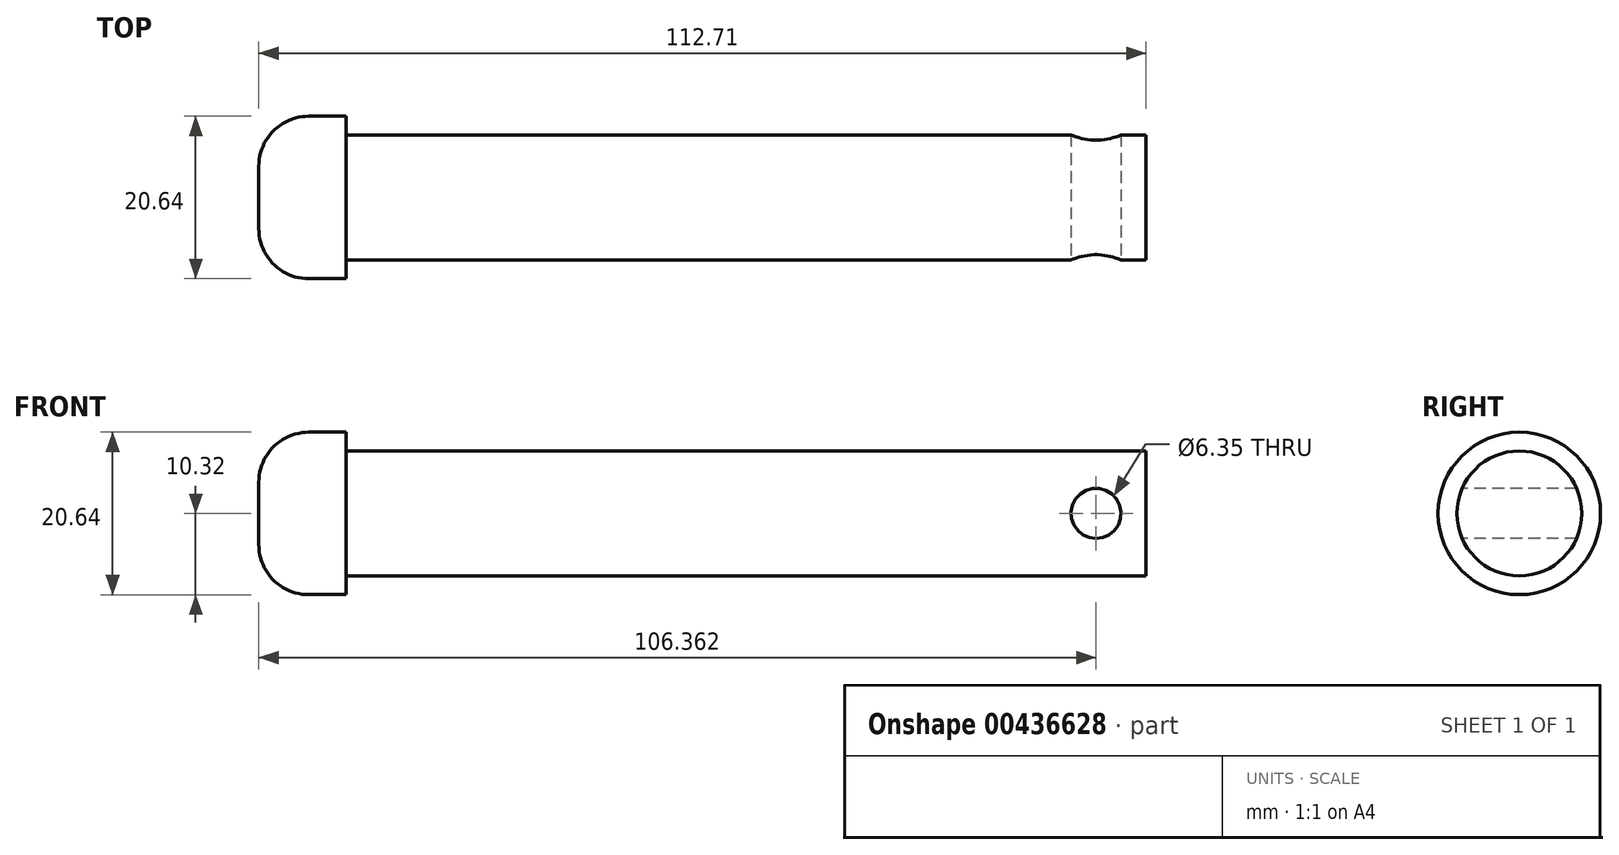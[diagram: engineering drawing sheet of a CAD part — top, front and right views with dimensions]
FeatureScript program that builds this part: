
annotation { "Feature Type Name" : "Feature", "Feature Type Description" : "" }
export const myFeature = defineFeature(function(context is Context, id is Id, definition is map)
    precondition{}
    {
        {
            var Q0;
            Q0=qCreatedBy(makeId("Front.planeOp"),FACE);
            var sketch = newSketch(context, id + "F0", { "sketchPlane" : qUnion([Q0])});
            skLineSegment(sketch, "E0", {"start": v(0, 3.97) * mm, "end": v(0, 0) * mm});
            skLineSegment(sketch, "E1", {"start": v(6.35, 10.32) * mm, "end": v(11.11, 10.32) * mm});
            skLineSegment(sketch, "E2", {"start": v(11.11, 10.32) * mm, "end": v(11.11, 7.94) * mm});
            skLineSegment(sketch, "E3", {"start": v(11.11, 7.94) * mm, "end": v(112.71, 7.94) * mm});
            skLineSegment(sketch, "E4", {"start": v(112.71, 7.94) * mm, "end": v(112.71, 0) * mm});
            skLineSegment(sketch, "E5", {"start": v(-31.62, 0) * mm, "end": v(102.7, 0) * mm, "construction": true});
            skPoint(sketch, "E6.visualSharp", {"position": v(0, 10.32) * mm});
            skArc(sketch, "E6.filletArc", {"start": v(6.35, 10.32) * mm, "mid": v(1.86, 8.46) * mm, "end": v(0, 3.97) * mm});
            skLineSegment(sketch, "E7", {"start": v(0, 0) * mm, "end": v(112.71, 0) * mm});
            skSolve(sketch);
        }
        {
            var Q0;
            Q0=makeQuery(id+"F0.imprint","IMPRINT",FACE,{"disambiguationData":[TD([[makeQuery(id+"F0.imprint","IMPRINT",EDGE,{"derivedFrom":sQuery(id+"F0.wireOp",EDGE,"E0")}),1.0]])]});
            var Q1;
            Q1=sQuery(id+"F0.wireOp",EDGE,"E5");
            revolve(context, id + "F1", {"surfaceOperationType" : NewSurfaceOperationType.NEW, "entities" : qUnion([Q0]), "axis" : qUnion([Q1]), "revolveType" : RevolveType.FULL});
        }
        {
            var Q0;
            Q0=qCreatedBy(makeId("Front.planeOp"),FACE);
            var sketch = newSketch(context, id + "F2", { "sketchPlane" : qUnion([Q0])});
            skCircle(sketch, "E8", {"center": v(106.36, 0) * mm, "radius": 3.17 * mm});
            skSolve(sketch);
        }
        {
            var Q0;
            Q0 = qSketchRegion(id + "F2", true);
            extrude(context, id + "F3", {"entities" : qUnion([Q0]), "operationType" : NewBodyOperationType.REMOVE, "oppositeDirection" : true, "depth" : 25.4 * mm, "offsetDistance" : 25.4 * mm, "symmetric" : true});
        }
    });
